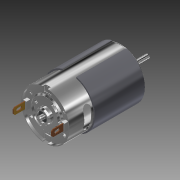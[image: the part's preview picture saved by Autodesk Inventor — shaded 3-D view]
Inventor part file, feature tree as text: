
AUTODESK INVENTOR PART (.ipt)
format: ipt  version: 2018 (Build 220112000, 112)  size: 926,720 bytes
history: native  units: mm (DEFAULTED — no unit token found)
features: extrude x24, sketch x24, fillet x7, plane x6, mirror x4, projected_geometry x3, chamfer x2, pattern_circular x2, shell x1, revolve x1
ambient origin geometry x8: Origin, YZ Plane, XZ Plane, XY Plane, X Axis, Y Axis, Z Axis, Center Point
bodies: Solid1 (feature_tree)
feature tree (74):
  extrude  "Extrusion1"  Depth=56.896mm TaperAngle=0.0deg
  fillet  "Fillet1"  Radius=2.0mm
  shell  "Shell1"  Thickness=0.62mm
  extrude  "Extrusion2"  Depth=4.572mm TaperAngle=0.0deg
  fillet  "Fillet2"  Radius=0.5mm
  plane  "Work Plane1"
  extrude  "Extrusion5"  Depth=0.62mm TaperAngle=0.0deg
  extrude  "Extrusion6"  Depth=1.016mm
  fillet  "Fillet4"  Radius=0.6096mm
  fillet  "Fillet5"  Radius=4.9276mm
  extrude  "Extrusion11"  Depth=11.43mm TaperAngle=0.0deg
  chamfer  "Chamfer1"  Distance=1.0mm
  sketch  "Sketch13"  dims[d61=3.0mm d69=18.0mm]
  mirror  "Mirror2"
  plane  "Work Plane2"
  plane  "Work Plane3"
  extrude  "Flux Ring"  Depth=18.0mm
  extrude  "Extrusion15"  Depth=1.016mm
  mirror  "Mirror3"
  sketch  "Sketch18"  dims[d83=0.254mm d93=2.413mm]
  extrude  "Extrusion16"  Depth=0.254mm
  extrude  "Extrusion17"  Depth=2.413mm
  chamfer  "Chamfer2"  Distance=2.921mm
  extrude  "Extrusion18"  Depth=3.429mm TaperAngle=0.0deg
  extrude  "Extrusion19"  Depth=3.429mm TaperAngle=0.0deg
  extrude  "Extrusion20"  Depth=1.397mm TaperAngle=0.0deg
  fillet  "Fillet9"  Radius=3.175mm
  extrude  "Extrusion21"  Depth=1.016mm
  extrude  "Extrusion22"  Depth=3.8862mm TaperAngle=0.0deg
  extrude  "Extrusion24"  Depth=0.508mm
  extrude  "Extrusion25"  Depth=1.016mm
  extrude  "Extrusion26"  Depth=3.8862mm TaperAngle=0.0deg
  plane  "Work Plane4"
  extrude  "Extrusion29"  Depth=1.860192mm
  fillet  "Fillet10"  Radius=3.699166mm
  extrude  "Extrusion30"  Depth=0.381mm
  fillet  "Fillet11"  Radius=0.6096mm
  mirror  "Mirror4"
  extrude  "Extrusion31"  Depth=1.27mm TaperAngle=0.0deg
  sketch  "Sketch29"  dims[d153=1.27mm d154=0.0mm d155=0.381mm d156=0.6096mm d157=0.0mm]
  extrude  "Extrusion32"  Depth=0.785398mm
  pattern_circular  "Circular Pattern4"  Count=40 Angle=360.0deg
  extrude  "Extrusion34"  Depth=2.949849mm
  pattern_circular  "Circular Pattern5"  [2 undecoded]
  revolve  "Revolution1"  [1 undecoded]
  extrude  "Extrusion35"  Depth=10.0076mm TaperAngle=0.0deg
  plane  "Work Plane6"
  extrude  "Extrusion36"  Depth=400.0mm TaperAngle=360.0deg
  mirror  "Mirror5"
  sketch  "Sketch1"  dims[d0=35.7886mm d1=56.896mm d2=0.0mm d3=2.0mm d4=0.62mm]
  sketch  "Sketch2"  dims[d5=13.0mm d6=4.572mm d7=0.0mm d8=0.5mm]
  sketch  "Sketch6"  dims[d30=-1.905mm d31=0.62mm d32=0.0mm]
  sketch  "Sketch7"  dims[d33=24.13mm d34=1.016mm d35=-7.853982mm d54=0.6096mm d55=4.9276mm]
  sketch  "Sketch12"  dims[d56=13.843mm d57=11.43mm d58=0.0mm d59=1.0mm d60=2.0mm]
  sketch  "Sketch15"  dims[d75=45.0deg d76=1.016mm]
  sketch  "Sketch17"  dims[d77=36.8808mm d78=0.0mm d82=0.254mm]
  sketch  "Sketch19"  dims[d95=5.588mm d96=2.921mm d97=0.0mm]
  sketch  "Sketch20"  dims[d102=25.4mm d103=0.0mm d104=3.429mm d105=0.0mm]
  sketch  "Sketch21"  dims[d106=0.508mm d107=1.27mm d108=45.0deg d109=3.429mm d110=0.0mm]
  sketch  "Sketch22"  dims[d111=3.6576mm d114=1.397mm d115=0.0mm d116=3.175mm]
  sketch  "Sketch23"  dims[d117=3.8862mm d118=77.0128mm d119=0.0mm d120=0.0mm d121=1.016mm]
  sketch  "Sketch24"  dims[d123=3.8862mm d124=0.0mm d125=3.8862mm d126=0.0mm]
  sketch  "Sketch25"  dims[d129=3.8862mm d130=0.0mm d137=0.508mm]
  projected_geometry  "Projected Loop1"
  sketch  "Sketch26"  dims[d139=0.508mm d140=1.016mm]
  projected_geometry  "Projected Loop2"
  sketch  "Sketch27"  dims[d141=0.508mm d142=3.8862mm d143=0.0mm]
  plane  "Work Plane5"
  sketch  "Sketch28"  dims[d144=0.6096mm d145=0.0mm d150=1.860192mm d152=3.699166mm]
  sketch  "Sketch30"  dims[d158=0.381mm d159=1.27mm d160=0.0mm]
  sketch  "Sketch31"  dims[d162=1.570796mm d163=0.785398mm]
  projected_geometry  "Projected Loop3"
  sketch  "Sketch32"  dims[d165=10.0076mm d166=0.0mm d167=400.0mm d168=360.0deg]
  sketch  "Sketch33"  dims[d170=3.200082mm d172=2.949849mm d173=1.570796mm d174=14.57284mm d178=10.0076mm d179=0.0mm d180=400.0mm d181=360.0deg d186=45.0deg d187=90.0deg d188=0.127mm d189=5.08mm d190=5.08mm d191=10.0076mm d192=0.0mm d193=1.27mm d194=5.715mm d195=10.668mm d196=5.334mm d197=10.0076mm d198=0.0mm]
note: 3 required parameter values undecoded (feature->parameter linkage not recoverable at this tier; creation-order binding heuristic only, values carry confidence <= 0.55)